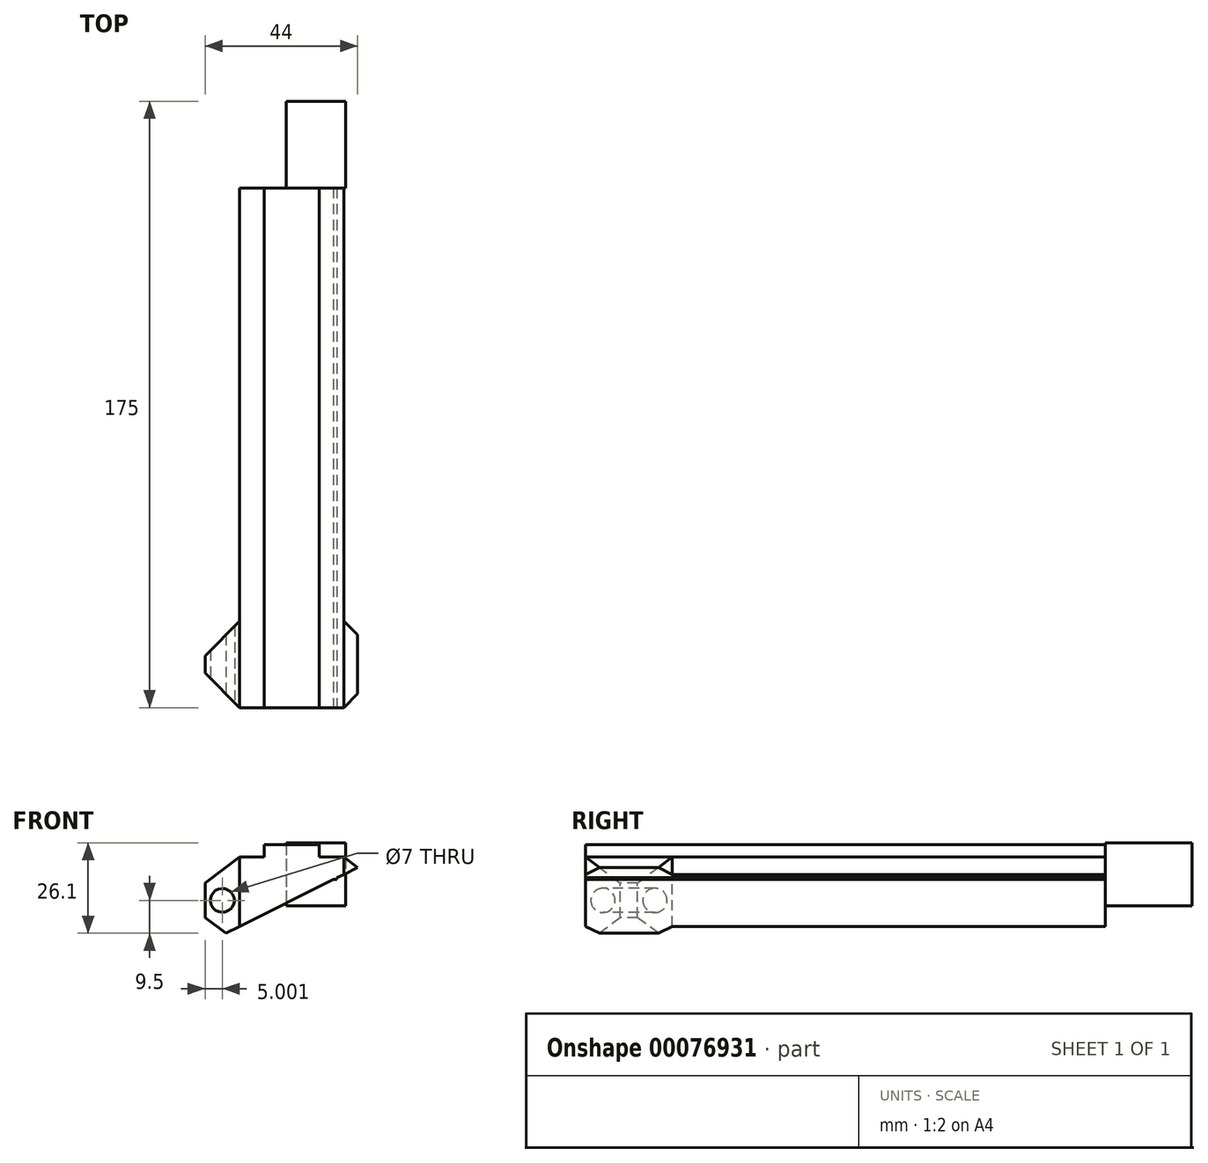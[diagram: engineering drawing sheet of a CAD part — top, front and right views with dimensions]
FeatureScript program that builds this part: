
annotation { "Feature Type Name" : "Feature", "Feature Type Description" : "" }
export const myFeature = defineFeature(function(context is Context, id is Id, definition is map)
    precondition{}
    {
        {
            var Q0;
            Q0=qCreatedBy(makeId("Top.planeOp"),FACE);
            var sketch = newSketch(context, id + "F0", { "sketchPlane" : qUnion([Q0])});
            skLineSegment(sketch, "E0.bottom", {"start": v(-67.09, 74.78) * mm, "end": v(-17.09, 74.78) * mm});
            skLineSegment(sketch, "E0.top", {"start": v(-67.09, -75.22) * mm, "end": v(-17.09, -75.22) * mm});
            skLineSegment(sketch, "E0.left", {"start": v(-67.09, 74.78) * mm, "end": v(-67.09, -75.22) * mm});
            skLineSegment(sketch, "E0.right", {"start": v(-17.09, 74.78) * mm, "end": v(-17.09, -75.22) * mm});
            skSolve(sketch);
        }
        {
            var Q0;
            Q0=makeQuery(id+"F0.imprint","IMPRINT",FACE,{"disambiguationData":[TD([[makeQuery(id+"F0.imprint","IMPRINT",EDGE,{"derivedFrom":sQuery(id+"F0.wireOp",EDGE,"E0.bottom")}),-1.0]])]});
            extrude(context, id + "F1", {"entities" : qUnion([Q0]), "depth" : 25 * mm});
        }
        {
            var Q0;
            Q0=makeQuery(id+"F1.opExtrude","SWEPT_FACE",FACE,{"disambiguationData":[OSD([sQuery(id+"F0.wireOp",EDGE,"E0.top")])]});
            var sketch = newSketch(context, id + "F2", { "sketchPlane" : qUnion([Q0])});
            skLineSegment(sketch, "E1", {"start": v(-67.09, 25) * mm, "end": v(-17.09, 0) * mm});
            skLineSegment(sketch, "E2", {"start": v(-67.09, 0) * mm, "end": v(-17.09, 25) * mm});
            skCircle(sketch, "E3", {"center": v(-42.09, 12.5) * mm, "radius": 5.05 * mm});
            skSolve(sketch);
        }
        {
            var Q0;
            {var subQ0=sQuery(id+"F2.wireOp",EDGE,"E3");var subQ1=sQuery(id+"F2.wireOp",EDGE,"E1");var subQ2=makeQuery(id+"F2.imprint","INTERSECT",VERTEX,{"disambiguationData":[OD(0.0)],"derivedFrom":[subQ1,subQ0]});Q0=makeQuery(id+"F2.imprint","IMPRINT",FACE,{"disambiguationData":[TD([[makeQuery(id+"F2.imprint","IMPRINT",EDGE,{"disambiguationData":[TD([[subQ2,-1.0]])],"derivedFrom":subQ1}),1.0]])]});}
            var Q1;
            {var subQ0=sQuery(id+"F2.wireOp",EDGE,"E2");var subQ1=sQuery(id+"F2.wireOp",EDGE,"E1");var subQ2=makeQuery(id+"F2.imprint","INTERSECT",VERTEX,{"derivedFrom":[subQ1,subQ0]});Q1=makeQuery(id+"F2.imprint","IMPRINT",FACE,{"disambiguationData":[TD([[makeQuery(id+"F2.imprint","IMPRINT",EDGE,{"disambiguationData":[TD([[subQ2,-1.0]])],"derivedFrom":subQ1}),1.0]])]});}
            var Q2;
            {var subQ0=sQuery(id+"F2.wireOp",EDGE,"E2");var subQ1=sQuery(id+"F2.wireOp",EDGE,"E1");var subQ2=makeQuery(id+"F2.imprint","INTERSECT",VERTEX,{"derivedFrom":[subQ1,subQ0]});Q2=makeQuery(id+"F2.imprint","IMPRINT",FACE,{"disambiguationData":[TD([[makeQuery(id+"F2.imprint","IMPRINT",EDGE,{"disambiguationData":[TD([[subQ2,-1.0]])],"derivedFrom":subQ1}),-1.0]])]});}
            var Q3;
            {var subQ0=sQuery(id+"F2.wireOp",EDGE,"E3");var subQ1=sQuery(id+"F2.wireOp",EDGE,"E1");var subQ2=makeQuery(id+"F2.imprint","INTERSECT",VERTEX,{"disambiguationData":[OD(0.0)],"derivedFrom":[subQ1,subQ0]});Q3=makeQuery(id+"F2.imprint","IMPRINT",FACE,{"disambiguationData":[TD([[makeQuery(id+"F2.imprint","IMPRINT",EDGE,{"disambiguationData":[TD([[subQ2,-1.0]])],"derivedFrom":subQ1}),-1.0]])]});}
            extrude(context, id + "F3", {"entities" : qUnion([Q0, Q1, Q2, Q3]), "operationType" : NewBodyOperationType.REMOVE, "oppositeDirection" : true, "depth" : 150 * mm});
        }
        {
            var Q0;
            Q0=makeQuery(id+"F1.opExtrude","CAP_FACE",FACE,{"disambiguationData":[OSD([sQuery(id+"F0.wireOp",EDGE,"E0.bottom"),sQuery(id+"F0.wireOp",EDGE,"E0.top"),sQuery(id+"F0.wireOp",EDGE,"E0.left"),sQuery(id+"F0.wireOp",EDGE,"E0.right")])],"isStart":false});
            var sketch = newSketch(context, id + "F4", { "sketchPlane" : qUnion([Q0])});
            skLineSegment(sketch, "E4", {"start": v(-10, -75.22) * mm, "end": v(-10, -65.22) * mm});
            skLineSegment(sketch, "E5", {"start": v(-10, -65.22) * mm, "end": v(-77.2, -65.22) * mm});
            skLineSegment(sketch, "E6", {"start": v(-17.09, -81.58) * mm, "end": v(-27.09, -81.58) * mm});
            skLineSegment(sketch, "E7", {"start": v(-67.09, -81.94) * mm, "end": v(-57.09, -81.94) * mm});
            skLineSegment(sketch, "E8", {"start": v(-27.09, -81.58) * mm, "end": v(-27.09, 83.34) * mm});
            skLineSegment(sketch, "E9", {"start": v(-57.09, -81.94) * mm, "end": v(-57.09, 84.92) * mm});
            skLineSegment(sketch, "E10", {"start": v(-17.09, -65.22) * mm, "end": v(-27.09, -75.22) * mm});
            skLineSegment(sketch, "E11", {"start": v(-10, -65.22) * mm, "end": v(-10, -60.22) * mm});
            skLineSegment(sketch, "E12", {"start": v(-10, -60.22) * mm, "end": v(-10, -50.22) * mm});
            skLineSegment(sketch, "E13", {"start": v(-10, -60.22) * mm, "end": v(-78.08, -60.22) * mm});
            skLineSegment(sketch, "E14", {"start": v(-10, -50.22) * mm, "end": v(-79.9, -50.22) * mm});
            skLineSegment(sketch, "E15", {"start": v(-17.09, -60.22) * mm, "end": v(-27.09, -50.22) * mm});
            skLineSegment(sketch, "E16", {"start": v(-57.09, -75.22) * mm, "end": v(-67.09, -65.22) * mm});
            skLineSegment(sketch, "E17", {"start": v(-67.09, -60.22) * mm, "end": v(-57.09, -50.22) * mm});
            skSolve(sketch);
        }
        {
            var Q0;
            {var subQ0=sQuery(id+"F4.wireOp",EDGE,"E10");Q0=makeQuery(id+"F4.imprint","IMPRINT",FACE,{"disambiguationData":[TD([[makeQuery(id+"F4.imprint","IMPRINT",EDGE,{"derivedFrom":subQ0}),1.0]])]});}
            var Q1;
            {var subQ0=sQuery(id+"F4.wireOp",EDGE,"E16");Q1=makeQuery(id+"F4.imprint","IMPRINT",FACE,{"disambiguationData":[TD([[makeQuery(id+"F4.imprint","IMPRINT",EDGE,{"derivedFrom":subQ0}),1.0]])]});}
            var Q2;
            {var subQ0=sQuery(id+"F4.wireOp",EDGE,"E17");Q2=makeQuery(id+"F4.imprint","IMPRINT",FACE,{"disambiguationData":[TD([[makeQuery(id+"F4.imprint","IMPRINT",EDGE,{"derivedFrom":subQ0}),1.0]])]});}
            var Q3;
            {var subQ0=sQuery(id+"F4.wireOp",EDGE,"E15");Q3=makeQuery(id+"F4.imprint","IMPRINT",FACE,{"disambiguationData":[TD([[makeQuery(id+"F4.imprint","IMPRINT",EDGE,{"derivedFrom":subQ0}),-1.0]])]});}
            var Q4;
            {var subQ3=makeQuery(id+"F1.opExtrude","CAP_EDGE",EDGE,{"disambiguationData":[OSD([sQuery(id+"F0.wireOp",EDGE,"E0.bottom")])],"isStart":false});var subQ5=makeQuery(id+"F1.opExtrude","CAP_EDGE",EDGE,{"disambiguationData":[OSD([sQuery(id+"F0.wireOp",EDGE,"E0.right")])],"isStart":false});var subQ7=makeQuery(id+"F4.imprint","INTERSECT",VERTEX,{"derivedFrom":[subQ3,subQ5]});Q4=makeQuery(id+"F4.imprint","IMPRINT",FACE,{"disambiguationData":[TD([[makeQuery(id+"F4.imprint","IMPRINT",EDGE,{"disambiguationData":[TD([[subQ7,1.0]])],"derivedFrom":subQ3}),-1.0]])]});}
            var Q5;
            {var subQ3=makeQuery(id+"F1.opExtrude","CAP_EDGE",EDGE,{"disambiguationData":[OSD([sQuery(id+"F0.wireOp",EDGE,"E0.bottom")])],"isStart":false});var subQ5=makeQuery(id+"F1.opExtrude","CAP_EDGE",EDGE,{"disambiguationData":[OSD([sQuery(id+"F0.wireOp",EDGE,"E0.left")])],"isStart":false});var subQ6=makeQuery(id+"F4.imprint","INTERSECT",VERTEX,{"derivedFrom":[subQ3,subQ5]});Q5=makeQuery(id+"F4.imprint","IMPRINT",FACE,{"disambiguationData":[TD([[makeQuery(id+"F4.imprint","IMPRINT",EDGE,{"disambiguationData":[TD([[subQ6,-1.0]])],"derivedFrom":subQ3}),-1.0]])]});}
            extrude(context, id + "F5", {"entities" : qUnion([Q0, Q1, Q2, Q3, Q4, Q5]), "operationType" : NewBodyOperationType.REMOVE, "oppositeDirection" : true, "depth" : 25 * mm});
        }
        {
            var Q0;
            Q0=makeQuery(id+"F1.opExtrude","SWEPT_FACE",FACE,{"disambiguationData":[OSD([sQuery(id+"F0.wireOp",EDGE,"E0.top")])]});
            var sketch = newSketch(context, id + "F6", { "sketchPlane" : qUnion([Q0])});
            skLineSegment(sketch, "E18", {"start": v(-50.09, 23.53) * mm, "end": v(-55.09, 23.53) * mm});
            skLineSegment(sketch, "E19", {"start": v(-55.09, 23.53) * mm, "end": v(-55.09, 18.53) * mm});
            skLineSegment(sketch, "E20", {"start": v(-34.09, 25) * mm, "end": v(-34.09, 23.53) * mm});
            skLineSegment(sketch, "E21", {"start": v(-34.09, 23.53) * mm, "end": v(-29.09, 23.53) * mm});
            skLineSegment(sketch, "E22", {"start": v(-29.09, 23.53) * mm, "end": v(-29.09, 18.53) * mm});
            skLineSegment(sketch, "E23", {"start": v(-55.09, 18.53) * mm, "end": v(-29.09, 18.53) * mm});
            skPoint(sketch, "E24.startSnap0", {"position": v(-50.09, 24.78) * mm});
            skPoint(sketch, "E25.orphan", {"position": v(-50.09, 26.02) * mm});
            skPoint(sketch, "E26.start.orphan", {"position": v(-27.09, 26.02) * mm});
            skPoint(sketch, "E24.start.orphan", {"position": v(-50.09, 25) * mm});
            skLineSegment(sketch, "E27", {"start": v(-50.09, 23.53) * mm, "end": v(-50.09, 25) * mm});
            skLineSegment(sketch, "E28", {"start": v(-34.09, 25) * mm, "end": v(-50.09, 25) * mm});
            skLineSegment(sketch, "E29", {"start": v(-42.09, 12.5) * mm, "end": v(-32.65, 12.5) * mm});
            skPoint(sketch, "E29.endSnap0", {"position": v(-42.09, 12.5) * mm});
            skLineSegment(sketch, "E30.MirrorCS", {"start": v(-50.09, 1.47) * mm, "end": v(-50.09, 0) * mm});
            skPoint(sketch, "E31.MirrorP", {"position": v(-50.09, 0) * mm});
            skLineSegment(sketch, "E32.MirrorCS", {"start": v(-29.09, 1.47) * mm, "end": v(-29.09, 6.47) * mm});
            skPoint(sketch, "E33.MirrorP", {"position": v(-50.09, 0.22) * mm});
            skLineSegment(sketch, "E34.MirrorCS", {"start": v(-55.09, 6.47) * mm, "end": v(-29.09, 6.47) * mm});
            skLineSegment(sketch, "E35.MirrorCS", {"start": v(-34.09, 0) * mm, "end": v(-50.09, 0) * mm});
            skLineSegment(sketch, "E36.MirrorCS", {"start": v(-34.09, 1.47) * mm, "end": v(-29.09, 1.47) * mm});
            skPoint(sketch, "E37.MirrorP", {"position": v(-50.09, -1.02) * mm});
            skLineSegment(sketch, "E38.MirrorCS", {"start": v(-34.09, 0) * mm, "end": v(-34.09, 1.47) * mm});
            skLineSegment(sketch, "E39.MirrorCS", {"start": v(-50.09, 1.47) * mm, "end": v(-55.09, 1.47) * mm});
            skLineSegment(sketch, "E40.MirrorCS", {"start": v(-55.09, 1.47) * mm, "end": v(-55.09, 6.47) * mm});
            skSolve(sketch);
        }
        {
            var Q0;
            Q0=makeQuery(id+"F6.imprint","IMPRINT",FACE,{"disambiguationData":[TD([[makeQuery(id+"F6.imprint","IMPRINT",EDGE,{"derivedFrom":sQuery(id+"F6.wireOp",EDGE,"E30.MirrorCS")}),1.0]])]});
            var Q1;
            Q1=makeQuery(id+"F6.imprint","IMPRINT",FACE,{"disambiguationData":[TD([[makeQuery(id+"F6.imprint","IMPRINT",EDGE,{"derivedFrom":sQuery(id+"F6.wireOp",EDGE,"E18")}),1.0]])]});
            extrude(context, id + "F7", {"entities" : qUnion([Q0, Q1]), "operationType" : NewBodyOperationType.REMOVE, "oppositeDirection" : true, "depth" : 150 * mm});
        }
        {
            var Q0;
            Q0=makeQuery(id+"F1.opExtrude","SWEPT_FACE",FACE,{"disambiguationData":[OSD([sQuery(id+"F0.wireOp",EDGE,"E0.top")])]});
            var sketch = newSketch(context, id + "F8", { "sketchPlane" : qUnion([Q0])});
            skLineSegment(sketch, "E41", {"start": v(-42.09, 12.5) * mm, "end": v(-69.22, 12.5) * mm});
            skLineSegment(sketch, "E42", {"start": v(-69.22, 12.5) * mm, "end": v(-69.22, 17.5) * mm});
            skLineSegment(sketch, "E43", {"start": v(-69.22, 12.5) * mm, "end": v(-69.22, 7.5) * mm});
            skLineSegment(sketch, "E44", {"start": v(-69.22, 17.5) * mm, "end": v(-54.55, 17.5) * mm});
            skLineSegment(sketch, "E45", {"start": v(-69.22, 7.5) * mm, "end": v(-54.95, 7.5) * mm});
            skLineSegment(sketch, "E46", {"start": v(-57.09, 0) * mm, "end": v(-67.09, 7.5) * mm});
            skLineSegment(sketch, "E47", {"start": v(-67.1, 17.5) * mm, "end": v(-57.09, 25) * mm});
            skLineSegment(sketch, "E48", {"start": v(-42.09, 12.5) * mm, "end": v(-42.09, 23.12) * mm});
            skLineSegment(sketch, "E49.MirrorCS", {"start": v(-17.08, 17.5) * mm, "end": v(-27.09, 25) * mm});
            skLineSegment(sketch, "E50", {"start": v(-57.09, 25) * mm, "end": v(-67.1, 25) * mm});
            skLineSegment(sketch, "E51", {"start": v(-67.1, 17.5) * mm, "end": v(-67.1, 25) * mm});
            skLineSegment(sketch, "E52.MirrorCS", {"start": v(-57.09, 0) * mm, "end": v(-67.1, 0) * mm});
            skLineSegment(sketch, "E53.MirrorCS", {"start": v(-67.1, 7.5) * mm, "end": v(-67.1, 0) * mm});
            skLineSegment(sketch, "E54.MirrorCS", {"start": v(-27.09, 25) * mm, "end": v(-17.08, 25) * mm});
            skLineSegment(sketch, "E55.MirrorCS", {"start": v(-17.08, 17.5) * mm, "end": v(-17.08, 25) * mm});
            skLineSegment(sketch, "E56.MirrorCS", {"start": v(-17.08, 7.5) * mm, "end": v(-27.09, 0) * mm});
            skLineSegment(sketch, "E57", {"start": v(-17.08, 7.5) * mm, "end": v(-17.08, 0) * mm});
            skLineSegment(sketch, "E58", {"start": v(-27.09, 0) * mm, "end": v(-17.08, 0) * mm});
            skPoint(sketch, "E59.orphan", {"position": v(-17.08, -2.38) * mm});
            skCircle(sketch, "E60", {"center": v(-62.09, 12.5) * mm, "radius": 3.5 * mm});
            skCircle(sketch, "E61.MirrorC", {"center": v(-22.09, 12.5) * mm, "radius": 3.5 * mm});
            skSolve(sketch);
        }
        {
            var Q0;
            Q0=makeQuery(id+"F8.imprint","IMPRINT",FACE,{"disambiguationData":[TD([[makeQuery(id+"F8.imprint","IMPRINT",EDGE,{"derivedFrom":sQuery(id+"F8.wireOp",EDGE,"E47")}),1.0]])]});
            var Q1;
            {var subQ0=sQuery(id+"F8.wireOp",EDGE,"E46");Q1=makeQuery(id+"F8.imprint","IMPRINT",FACE,{"disambiguationData":[TD([[makeQuery(id+"F8.imprint","IMPRINT",EDGE,{"derivedFrom":subQ0}),1.0]])]});}
            var Q2;
            Q2=makeQuery(id+"F8.imprint","IMPRINT",FACE,{"disambiguationData":[TD([[makeQuery(id+"F8.imprint","IMPRINT",EDGE,{"derivedFrom":sQuery(id+"F8.wireOp",EDGE,"E49.MirrorCS")}),-1.0]])]});
            var Q3;
            Q3=makeQuery(id+"F8.imprint","IMPRINT",FACE,{"disambiguationData":[TD([[makeQuery(id+"F8.imprint","IMPRINT",EDGE,{"derivedFrom":sQuery(id+"F8.wireOp",EDGE,"E56.MirrorCS")}),1.0]])]});
            var Q4;
            {var subQ0=sQuery(id+"F8.wireOp",EDGE,"E60");var subQ1=sQuery(id+"F8.wireOp",EDGE,"E41");var subQ2=makeQuery(id+"F8.imprint","INTERSECT",VERTEX,{"disambiguationData":[OD(0.0)],"derivedFrom":[subQ1,subQ0]});Q4=makeQuery(id+"F8.imprint","IMPRINT",FACE,{"disambiguationData":[TD([[makeQuery(id+"F8.imprint","IMPRINT",EDGE,{"disambiguationData":[TD([[subQ2,-1.0]])],"derivedFrom":subQ1}),1.0]])]});}
            var Q5;
            {var subQ0=sQuery(id+"F8.wireOp",EDGE,"E60");var subQ1=sQuery(id+"F8.wireOp",EDGE,"E41");var subQ2=makeQuery(id+"F8.imprint","INTERSECT",VERTEX,{"disambiguationData":[OD(0.0)],"derivedFrom":[subQ1,subQ0]});Q5=makeQuery(id+"F8.imprint","IMPRINT",FACE,{"disambiguationData":[TD([[makeQuery(id+"F8.imprint","IMPRINT",EDGE,{"disambiguationData":[TD([[subQ2,-1.0]])],"derivedFrom":subQ1}),-1.0]])]});}
            var Q6;
            Q6=makeQuery(id+"F8.imprint","IMPRINT",FACE,{"disambiguationData":[TD([[makeQuery(id+"F8.imprint","IMPRINT",EDGE,{"derivedFrom":sQuery(id+"F8.wireOp",EDGE,"E61.MirrorC")}),-1.0]])]});
            extrude(context, id + "F9", {"entities" : qUnion([Q0, Q1, Q2, Q3, Q4, Q5, Q6]), "operationType" : NewBodyOperationType.REMOVE, "oppositeDirection" : true, "depth" : 25 * mm});
        }
        {
            var Q0;
            Q0=makeQuery(id+"F1.opExtrude","SWEPT_FACE",FACE,{"disambiguationData":[OSD([sQuery(id+"F0.wireOp",EDGE,"E0.bottom")])]});
            var sketch = newSketch(context, id + "F10", { "sketchPlane" : qUnion([Q0])});
            skLineSegment(sketch, "E62", {"start": v(34.09, 23.53) * mm, "end": v(29.09, 23.53) * mm});
            skLineSegment(sketch, "E63", {"start": v(29.09, 23.53) * mm, "end": v(29.09, 18.53) * mm});
            skLineSegment(sketch, "E64", {"start": v(29.09, 18.53) * mm, "end": v(55.09, 18.53) * mm});
            skLineSegment(sketch, "E65", {"start": v(55.09, 18.53) * mm, "end": v(55.09, 23.53) * mm});
            skLineSegment(sketch, "E66", {"start": v(55.09, 23.53) * mm, "end": v(50.09, 23.53) * mm});
            skLineSegment(sketch, "E67", {"start": v(50.09, 23.53) * mm, "end": v(50.09, 28.53) * mm});
            skLineSegment(sketch, "E68", {"start": v(50.09, 28.53) * mm, "end": v(34.09, 28.53) * mm});
            skLineSegment(sketch, "E69", {"start": v(34.09, 23.53) * mm, "end": v(34.09, 28.53) * mm});
            skLineSegment(sketch, "E70", {"start": v(42.09, 12.5) * mm, "end": v(14.57, 12.5) * mm});
            skLineSegment(sketch, "E71.MirrorCS", {"start": v(29.09, 6.47) * mm, "end": v(55.09, 6.47) * mm});
            skLineSegment(sketch, "E72.MirrorCS", {"start": v(29.09, 1.47) * mm, "end": v(29.09, 6.47) * mm});
            skLineSegment(sketch, "E73.MirrorCS", {"start": v(34.09, 1.47) * mm, "end": v(29.09, 1.47) * mm});
            skLineSegment(sketch, "E74.MirrorCS", {"start": v(34.09, 1.47) * mm, "end": v(34.09, -3.53) * mm});
            skLineSegment(sketch, "E75.MirrorCS", {"start": v(50.09, -3.53) * mm, "end": v(34.09, -3.53) * mm});
            skLineSegment(sketch, "E76.MirrorCS", {"start": v(50.09, 1.47) * mm, "end": v(50.09, -3.53) * mm});
            skLineSegment(sketch, "E77.MirrorCS", {"start": v(55.09, 1.47) * mm, "end": v(50.09, 1.47) * mm});
            skLineSegment(sketch, "E78.MirrorCS", {"start": v(55.09, 6.47) * mm, "end": v(55.09, 1.47) * mm});
            skSolve(sketch);
        }
        {
            var Q0;
            {var subQ1=sQuery(id+"F10.wireOp",EDGE,"E62");Q0=makeQuery(id+"F10.imprint","IMPRINT",FACE,{"disambiguationData":[TD([[makeQuery(id+"F10.imprint","IMPRINT",EDGE,{"derivedFrom":subQ1}),1.0]])]});}
            var Q1;
            Q1=makeQuery(id+"F10.imprint","IMPRINT",FACE,{"disambiguationData":[TD([[makeQuery(id+"F10.imprint","IMPRINT",EDGE,{"derivedFrom":sQuery(id+"F10.wireOp",EDGE,"E71.MirrorCS")}),1.0]])]});
            extrude(context, id + "F11", {"entities" : qUnion([Q0, Q1]), "oppositeDirection" : true, "depth" : 150 * mm});
        }
        {
            var Q0;
            Q0=makeQuery(id+"F11.opExtrude","CAP_FACE",FACE,{"disambiguationData":[OSD([sQuery(id+"F10.wireOp",EDGE,"E62"),sQuery(id+"F10.wireOp",EDGE,"E63"),sQuery(id+"F10.wireOp",EDGE,"E64"),sQuery(id+"F10.wireOp",EDGE,"E65"),sQuery(id+"F10.wireOp",EDGE,"E66"),sQuery(id+"F10.wireOp",EDGE,"E67"),sQuery(id+"F10.wireOp",EDGE,"E68"),sQuery(id+"F10.wireOp",EDGE,"E69")])],"isStart":true});
            var sketch = newSketch(context, id + "F12", { "sketchPlane" : qUnion([Q0])});
            skLineSegment(sketch, "E79.bottom", {"start": v(26.53, 29.1) * mm, "end": v(43.7, 29.1) * mm});
            skLineSegment(sketch, "E79.top", {"start": v(26.53, 10.9) * mm, "end": v(43.7, 10.9) * mm});
            skLineSegment(sketch, "E79.left", {"start": v(26.53, 29.1) * mm, "end": v(26.53, 10.9) * mm});
            skLineSegment(sketch, "E79.right", {"start": v(43.7, 29.1) * mm, "end": v(43.7, 10.9) * mm});
            skSolve(sketch);
        }
        {
            var Q0;
            {var subQ1=sQuery(id+"F12.wireOp",EDGE,"E79.bottom");Q0=makeQuery(id+"F12.imprint","IMPRINT",FACE,{"disambiguationData":[TD([[makeQuery(id+"F12.imprint","IMPRINT",EDGE,{"derivedFrom":subQ1}),-1.0]])]});}
            var Q1;
            Q1=makeQuery(id+"F12.imprint","IMPRINT",FACE,{"disambiguationData":[TD([[makeQuery(id+"F12.imprint","IMPRINT",EDGE,{"derivedFrom":makeQuery(id+"F11.opExtrude","CAP_EDGE",EDGE,{"disambiguationData":[OSD([sQuery(id+"F10.wireOp",EDGE,"E62")])],"isStart":true})}),1.0]])]});
            extrude(context, id + "F13", {"entities" : qUnion([Q0, Q1]), "operationType" : NewBodyOperationType.ADD, "depth" : 25 * mm});
        }
    });
